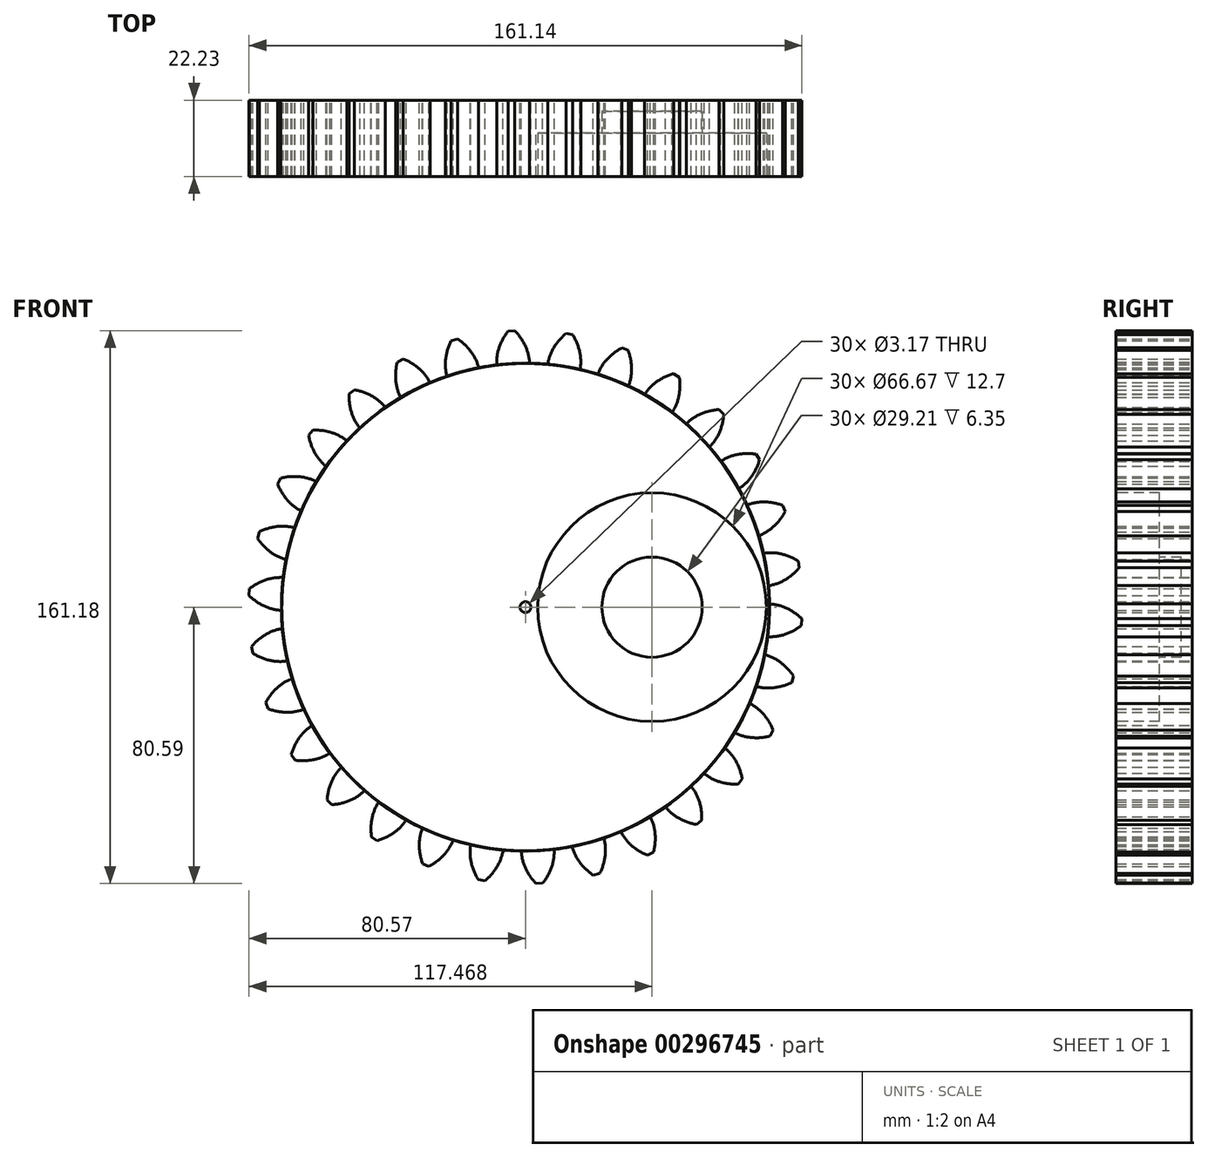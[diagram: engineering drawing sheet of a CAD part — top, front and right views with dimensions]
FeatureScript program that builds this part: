
annotation { "Feature Type Name" : "Feature", "Feature Type Description" : "" }
export const myFeature = defineFeature(function(context is Context, id is Id, definition is map)
    precondition{}
    {
        {
            var Q0;
            Q0=qCreatedBy(makeId("Front.planeOp"),FACE);
            var sketch = newSketch(context, id + "F0", { "sketchPlane" : qUnion([Q0])});
            skCircle(sketch, "E0", {"center": v(0, 0) * mm, "radius": 76.07 * mm, "construction": true});
            skCircle(sketch, "E1", {"center": v(0, 0) * mm, "radius": 80.65 * mm, "construction": true});
            skCircle(sketch, "E2", {"center": v(0, 0) * mm, "radius": 71.12 * mm});
            skLineSegment(sketch, "E3", {"start": v(0, 0) * mm, "end": v(0, 83.58) * mm, "construction": true});
            skLineSegment(sketch, "E4", {"start": v(0, 0) * mm, "end": v(-4.2, 83.24) * mm, "construction": true});
            skLineSegment(sketch, "E5", {"start": v(0, 76.07) * mm, "end": v(-81.86, 76.07) * mm, "construction": true});
            skLineSegment(sketch, "E6", {"start": v(-81.86, 76.07) * mm, "end": v(0, 76.07) * mm, "construction": true});
            skLineSegment(sketch, "E7", {"start": v(0, 76.07) * mm, "end": v(-77.07, 48.02) * mm, "construction": true});
            skCircle(sketch, "E8", {"center": v(0, 76.07) * mm, "radius": 14.6 * mm, "construction": true});
            skCircle(sketch, "E9", {"center": v(0, 0) * mm, "radius": 71.49 * mm, "construction": true});
            skCircle(sketch, "E10", {"center": v(-13.38, 70.22) * mm, "radius": 14.6 * mm, "construction": true});
            skArc(sketch, "E11", {"start": v(0, 76.07) * mm, "mid": v(-1.36, 78.46) * mm, "end": v(-3.1, 80.59) * mm});
            skArc(sketch, "E12", {"start": v(1.2, 71.1) * mm, "mid": v(0.84, 73.65) * mm, "end": v(0, 76.07) * mm});
            skArc(sketch, "E13.MirrorCS", {"start": v(-7.67, 75.69) * mm, "mid": v(-6.56, 78.2) * mm, "end": v(-5.05, 80.49) * mm});
            skArc(sketch, "E14.MirrorCS", {"start": v(-8.36, 70.63) * mm, "mid": v(-8.26, 73.2) * mm, "end": v(-7.67, 75.69) * mm});
            skLineSegment(sketch, "E15", {"start": v(-5.05, 80.49) * mm, "end": v(-3.1, 80.59) * mm});
            skCircle(sketch, "E16", {"center": v(0, 0) * mm, "radius": 1.59 * mm});
            skSolve(sketch);
        }
        {
            var Q0;
            {var subQ0=sQuery(id+"F0.wireOp",EDGE,"E2");var subQ1=makeQuery(id+"F0.imprint","INTERSECT",VERTEX,{"derivedFrom":[subQ0,sQuery(id+"F0.wireOp",EDGE,"E12")]});Q0=makeQuery(id+"F0.imprint","IMPRINT",FACE,{"disambiguationData":[TD([[makeQuery(id+"F0.imprint","IMPRINT",EDGE,{"disambiguationData":[TD([[subQ1,-1.0]])],"derivedFrom":subQ0}),1.0]])]});}
            var Q1;
            Q1=makeQuery(id+"F0.imprint","IMPRINT",FACE,{"disambiguationData":[TD([[makeQuery(id+"F0.imprint","IMPRINT",EDGE,{"derivedFrom":sQuery(id+"F0.wireOp",EDGE,"E11")}),1.0]])]});
            extrude(context, id + "F1", {"entities" : qUnion([Q0, Q1]), "depth" : 22.22 * mm});
        }
        {
            var Q0;
            Q0=makeQuery(id+"F1.opExtrude","SWEPT_BODY",BODY,{"disambiguationData":[OSD([sQuery(id+"F0.wireOp",EDGE,"E2"),sQuery(id+"F0.wireOp",EDGE,"E11"),sQuery(id+"F0.wireOp",EDGE,"E12"),sQuery(id+"F0.wireOp",EDGE,"E13.MirrorCS"),sQuery(id+"F0.wireOp",EDGE,"E14.MirrorCS"),sQuery(id+"F0.wireOp",EDGE,"E15")])]});
            var Q1;
            Q1=makeQuery(id+"F1.opExtrude","SWEPT_FACE",FACE,{"disambiguationData":[OSD([sQuery(id+"F0.wireOp",EDGE,"E2")])]});
            circularPattern(context, id + "F2", {"entities" : qUnion([Q0]), "axis" : qUnion([Q1]), "angle" : 360 * degree, "instanceCount" : 30, "equalSpace" : true});
        }
        {
            var Q0;
            {var subQ0=makeQuery(id+"F1.opExtrude","CAP_FACE",FACE,{"disambiguationData":[OSD([sQuery(id+"F0.wireOp",EDGE,"E2"),sQuery(id+"F0.wireOp",EDGE,"E11"),sQuery(id+"F0.wireOp",EDGE,"E12"),sQuery(id+"F0.wireOp",EDGE,"E13.MirrorCS"),sQuery(id+"F0.wireOp",EDGE,"E14.MirrorCS"),sQuery(id+"F0.wireOp",EDGE,"E15"),sQuery(id+"F0.wireOp",EDGE,"E16")])],"isStart":false});Q0=makeQuery(id+"FfTAEXdrTkSAiDa_0.boolean.opBoolean","MERGE",FACE,{"derivedFrom":[subQ0,makeQuery(id+"F2.opPattern","COPY",FACE,{"derivedFrom":subQ0,"instanceName":"1"}),makeQuery(id+"F2.opPattern","COPY",FACE,{"derivedFrom":subQ0,"instanceName":"2"}),makeQuery(id+"F2.opPattern","COPY",FACE,{"derivedFrom":subQ0,"instanceName":"3"}),makeQuery(id+"F2.opPattern","COPY",FACE,{"derivedFrom":subQ0,"instanceName":"4"}),makeQuery(id+"F2.opPattern","COPY",FACE,{"derivedFrom":subQ0,"instanceName":"5"}),makeQuery(id+"F2.opPattern","COPY",FACE,{"derivedFrom":subQ0,"instanceName":"6"}),makeQuery(id+"F2.opPattern","COPY",FACE,{"derivedFrom":subQ0,"instanceName":"7"}),makeQuery(id+"F2.opPattern","COPY",FACE,{"derivedFrom":subQ0,"instanceName":"8"}),makeQuery(id+"F2.opPattern","COPY",FACE,{"derivedFrom":subQ0,"instanceName":"9"}),makeQuery(id+"F2.opPattern","COPY",FACE,{"derivedFrom":subQ0,"instanceName":"10"}),makeQuery(id+"F2.opPattern","COPY",FACE,{"derivedFrom":subQ0,"instanceName":"11"}),makeQuery(id+"F2.opPattern","COPY",FACE,{"derivedFrom":subQ0,"instanceName":"12"}),makeQuery(id+"F2.opPattern","COPY",FACE,{"derivedFrom":subQ0,"instanceName":"13"}),makeQuery(id+"F2.opPattern","COPY",FACE,{"derivedFrom":subQ0,"instanceName":"14"}),makeQuery(id+"F2.opPattern","COPY",FACE,{"derivedFrom":subQ0,"instanceName":"15"}),makeQuery(id+"F2.opPattern","COPY",FACE,{"derivedFrom":subQ0,"instanceName":"16"}),makeQuery(id+"F2.opPattern","COPY",FACE,{"derivedFrom":subQ0,"instanceName":"17"}),makeQuery(id+"F2.opPattern","COPY",FACE,{"derivedFrom":subQ0,"instanceName":"18"}),makeQuery(id+"F2.opPattern","COPY",FACE,{"derivedFrom":subQ0,"instanceName":"19"}),makeQuery(id+"F2.opPattern","COPY",FACE,{"derivedFrom":subQ0,"instanceName":"20"}),makeQuery(id+"F2.opPattern","COPY",FACE,{"derivedFrom":subQ0,"instanceName":"21"}),makeQuery(id+"F2.opPattern","COPY",FACE,{"derivedFrom":subQ0,"instanceName":"22"}),makeQuery(id+"F2.opPattern","COPY",FACE,{"derivedFrom":subQ0,"instanceName":"23"}),makeQuery(id+"F2.opPattern","COPY",FACE,{"derivedFrom":subQ0,"instanceName":"24"}),makeQuery(id+"F2.opPattern","COPY",FACE,{"derivedFrom":subQ0,"instanceName":"25"}),makeQuery(id+"F2.opPattern","COPY",FACE,{"derivedFrom":subQ0,"instanceName":"26"}),makeQuery(id+"F2.opPattern","COPY",FACE,{"derivedFrom":subQ0,"instanceName":"27"}),makeQuery(id+"F2.opPattern","COPY",FACE,{"derivedFrom":subQ0,"instanceName":"28"}),makeQuery(id+"F2.opPattern","COPY",FACE,{"derivedFrom":subQ0,"instanceName":"29"})]});}
            var sketch = newSketch(context, id + "F3", { "sketchPlane" : qUnion([Q0])});
            skCircle(sketch, "E17", {"center": v(36.9, 0) * mm, "radius": 33.34 * mm});
            skCircle(sketch, "E18", {"center": v(36.9, 0) * mm, "radius": 14.6 * mm});
            skSolve(sketch);
        }
        {
            var Q0;
            Q0=makeQuery(id+"F3.imprint","IMPRINT",FACE,{"disambiguationData":[TD([[makeQuery(id+"F3.imprint","IMPRINT",EDGE,{"derivedFrom":sQuery(id+"F3.wireOp",EDGE,"E17")}),1.0]])]});
            extrude(context, id + "F4", {"entities" : qUnion([Q0]), "operationType" : NewBodyOperationType.REMOVE, "oppositeDirection" : true, "depth" : 12.7 * mm});
        }
        {
            var Q0;
            {var subQ0=makeQuery(id+"F1.opExtrude","CAP_FACE",FACE,{"disambiguationData":[OSD([sQuery(id+"F0.wireOp",EDGE,"E2"),sQuery(id+"F0.wireOp",EDGE,"E11"),sQuery(id+"F0.wireOp",EDGE,"E12"),sQuery(id+"F0.wireOp",EDGE,"E13.MirrorCS"),sQuery(id+"F0.wireOp",EDGE,"E14.MirrorCS"),sQuery(id+"F0.wireOp",EDGE,"E15"),sQuery(id+"F0.wireOp",EDGE,"E16")])],"isStart":false});Q0=makeQuery(id+"F4.boolean.opBoolean","SPLIT",FACE,{"disambiguationData":[TD([makeQuery(id+"F4.opExtrude","SWEPT_FACE",FACE,{"disambiguationData":[OSD([sQuery(id+"F3.wireOp",EDGE,"E18")])]})])],"derivedFrom":makeQuery(id+"FfTAEXdrTkSAiDa_0.boolean.opBoolean","MERGE",FACE,{"derivedFrom":[subQ0,makeQuery(id+"F2.opPattern","COPY",FACE,{"derivedFrom":subQ0,"instanceName":"1"}),makeQuery(id+"F2.opPattern","COPY",FACE,{"derivedFrom":subQ0,"instanceName":"2"}),makeQuery(id+"F2.opPattern","COPY",FACE,{"derivedFrom":subQ0,"instanceName":"3"}),makeQuery(id+"F2.opPattern","COPY",FACE,{"derivedFrom":subQ0,"instanceName":"4"}),makeQuery(id+"F2.opPattern","COPY",FACE,{"derivedFrom":subQ0,"instanceName":"5"}),makeQuery(id+"F2.opPattern","COPY",FACE,{"derivedFrom":subQ0,"instanceName":"6"}),makeQuery(id+"F2.opPattern","COPY",FACE,{"derivedFrom":subQ0,"instanceName":"7"}),makeQuery(id+"F2.opPattern","COPY",FACE,{"derivedFrom":subQ0,"instanceName":"8"}),makeQuery(id+"F2.opPattern","COPY",FACE,{"derivedFrom":subQ0,"instanceName":"9"}),makeQuery(id+"F2.opPattern","COPY",FACE,{"derivedFrom":subQ0,"instanceName":"10"}),makeQuery(id+"F2.opPattern","COPY",FACE,{"derivedFrom":subQ0,"instanceName":"11"}),makeQuery(id+"F2.opPattern","COPY",FACE,{"derivedFrom":subQ0,"instanceName":"12"}),makeQuery(id+"F2.opPattern","COPY",FACE,{"derivedFrom":subQ0,"instanceName":"13"}),makeQuery(id+"F2.opPattern","COPY",FACE,{"derivedFrom":subQ0,"instanceName":"14"}),makeQuery(id+"F2.opPattern","COPY",FACE,{"derivedFrom":subQ0,"instanceName":"15"}),makeQuery(id+"F2.opPattern","COPY",FACE,{"derivedFrom":subQ0,"instanceName":"16"}),makeQuery(id+"F2.opPattern","COPY",FACE,{"derivedFrom":subQ0,"instanceName":"17"}),makeQuery(id+"F2.opPattern","COPY",FACE,{"derivedFrom":subQ0,"instanceName":"18"}),makeQuery(id+"F2.opPattern","COPY",FACE,{"derivedFrom":subQ0,"instanceName":"19"}),makeQuery(id+"F2.opPattern","COPY",FACE,{"derivedFrom":subQ0,"instanceName":"20"}),makeQuery(id+"F2.opPattern","COPY",FACE,{"derivedFrom":subQ0,"instanceName":"21"}),makeQuery(id+"F2.opPattern","COPY",FACE,{"derivedFrom":subQ0,"instanceName":"22"}),makeQuery(id+"F2.opPattern","COPY",FACE,{"derivedFrom":subQ0,"instanceName":"23"}),makeQuery(id+"F2.opPattern","COPY",FACE,{"derivedFrom":subQ0,"instanceName":"24"}),makeQuery(id+"F2.opPattern","COPY",FACE,{"derivedFrom":subQ0,"instanceName":"25"}),makeQuery(id+"F2.opPattern","COPY",FACE,{"derivedFrom":subQ0,"instanceName":"26"}),makeQuery(id+"F2.opPattern","COPY",FACE,{"derivedFrom":subQ0,"instanceName":"27"}),makeQuery(id+"F2.opPattern","COPY",FACE,{"derivedFrom":subQ0,"instanceName":"28"}),makeQuery(id+"F2.opPattern","COPY",FACE,{"derivedFrom":subQ0,"instanceName":"29"})]})});}
            extrude(context, id + "F5", {"entities" : qUnion([Q0]), "operationType" : NewBodyOperationType.REMOVE, "oppositeDirection" : true, "depth" : 19.05 * mm});
        }
    });
